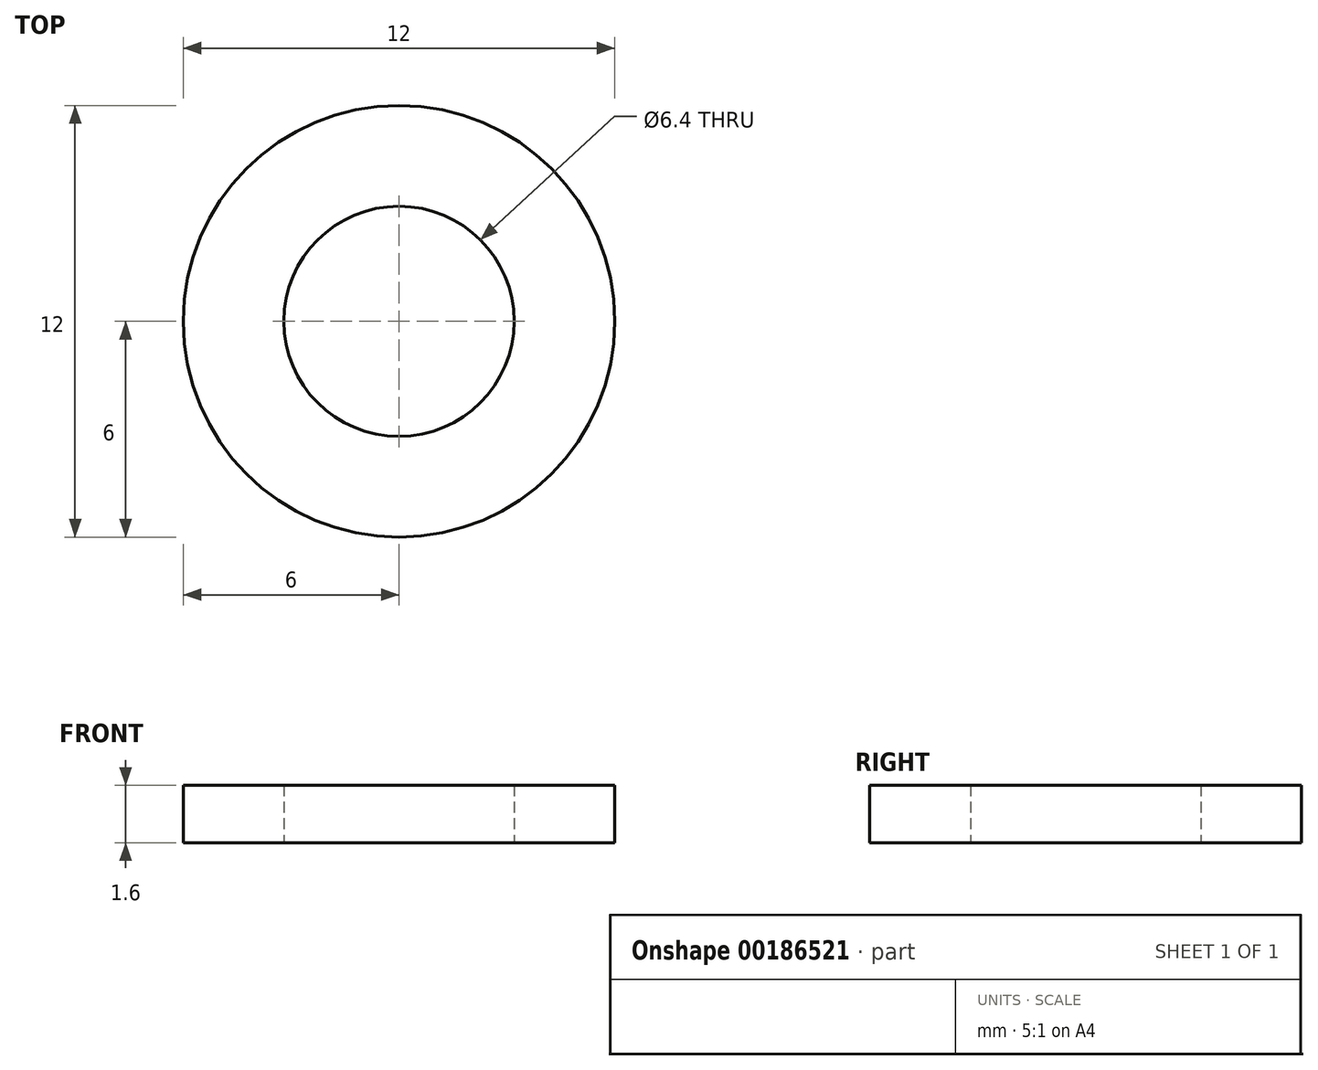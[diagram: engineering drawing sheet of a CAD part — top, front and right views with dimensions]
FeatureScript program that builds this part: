
annotation { "Feature Type Name" : "Feature", "Feature Type Description" : "" }
export const myFeature = defineFeature(function(context is Context, id is Id, definition is map)
    precondition{}
    {
        {
            var Q0;
            Q0=qCreatedBy(makeId("Top.planeOp"),FACE);
            var sketch = newSketch(context, id + "F0", { "sketchPlane" : qUnion([Q0])});
            skCircle(sketch, "E0", {"center": v(0, 0) * mm, "radius": 6 * mm});
            skCircle(sketch, "E1", {"center": v(0, 0) * mm, "radius": 3.2 * mm});
            skSolve(sketch);
        }
        {
            var Q0;
            Q0 = qSketchRegion(id + "F0", true);
            extrude(context, id + "F1", {"entities" : qUnion([Q0]), "depth" : 1.6 * mm});
        }
    });
